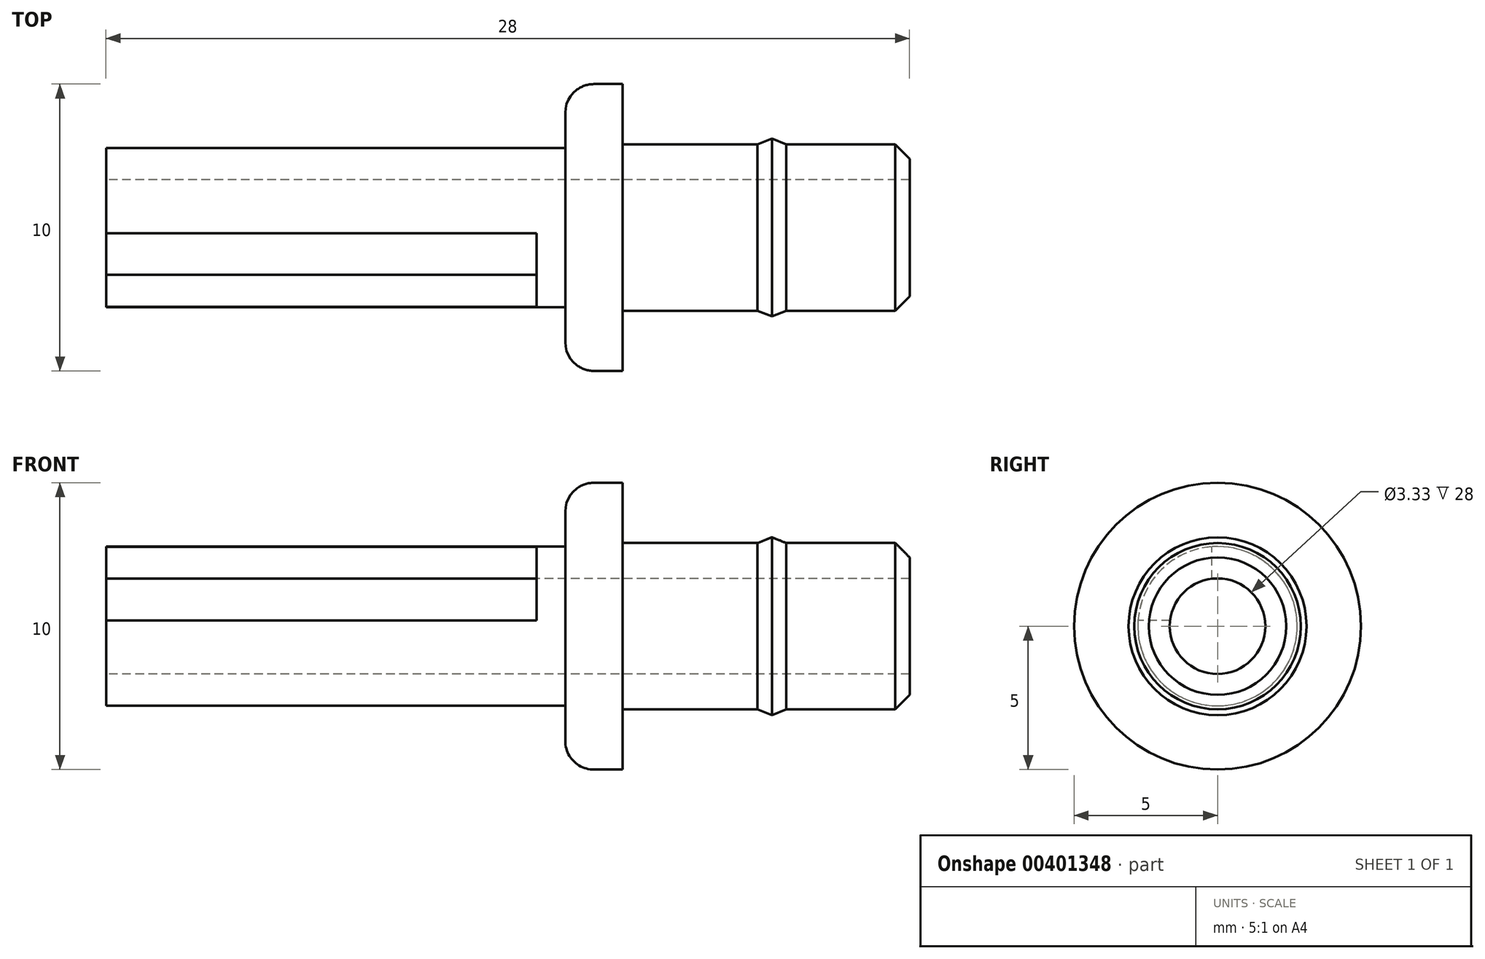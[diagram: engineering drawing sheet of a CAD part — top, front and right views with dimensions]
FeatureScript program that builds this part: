
annotation { "Feature Type Name" : "Feature", "Feature Type Description" : "" }
export const myFeature = defineFeature(function(context is Context, id is Id, definition is map)
    precondition{}
    {
        {
            var Q0;
            Q0=qCreatedBy(makeId("Front.planeOp"),FACE);
            var sketch = newSketch(context, id + "F0", { "sketchPlane" : qUnion([Q0])});
            skLineSegment(sketch, "E0", {"start": v(2.76, 1.67) * mm, "end": v(15.76, 1.67) * mm});
            skLineSegment(sketch, "E1", {"start": v(5.76, 2.9) * mm, "end": v(5.76, 5) * mm});
            skLineSegment(sketch, "E2", {"start": v(5.76, 5) * mm, "end": v(3.76, 5) * mm});
            skLineSegment(sketch, "E3", {"start": v(3.76, 5) * mm, "end": v(3.76, 2.78) * mm});
            skLineSegment(sketch, "E4", {"start": v(3.76, 2.78) * mm, "end": v(2.76, 2.78) * mm});
            skLineSegment(sketch, "E5", {"start": v(2.76, 2.78) * mm, "end": v(2.76, 1.67) * mm});
            skLineSegment(sketch, "E6", {"start": v(2.76, 0) * mm, "end": v(13.38, 0) * mm});
            skLineSegment(sketch, "E7", {"start": v(15.26, 2.9) * mm, "end": v(11.46, 2.9) * mm});
            skLineSegment(sketch, "E8", {"start": v(10.46, 2.9) * mm, "end": v(5.76, 2.9) * mm});
            skLineSegment(sketch, "E9", {"start": v(15.26, 2.9) * mm, "end": v(15.76, 2.4) * mm});
            skLineSegment(sketch, "E10", {"start": v(15.76, 2.4) * mm, "end": v(15.76, 1.67) * mm});
            skLineSegment(sketch, "E11", {"start": v(10.46, 2.9) * mm, "end": v(10.96, 3.1) * mm});
            skLineSegment(sketch, "E12", {"start": v(10.96, 3.1) * mm, "end": v(11.46, 2.9) * mm});
            skSolve(sketch);
        }
        {
            var Q0;
            Q0=makeQuery(id+"F0.imprint","IMPRINT",FACE,{"disambiguationData":[TD([[makeQuery(id+"F0.imprint","IMPRINT",EDGE,{"derivedFrom":sQuery(id+"F0.wireOp",EDGE,"E0")}),1.0]])]});
            var Q1;
            Q1=sQuery(id+"F0.wireOp",EDGE,"E6");
            revolve(context, id + "F1", {"entities" : qUnion([Q0]), "axis" : qUnion([Q1]), "revolveType" : RevolveType.FULL});
        }
        {
            var Q0;
            Q0=makeQuery(id+"F1.opRevolve","SWEPT_FACE",FACE,{"disambiguationData":[OSD([sQuery(id+"F0.wireOp",EDGE,"E5")])]});
            var sketch = newSketch(context, id + "F2", { "sketchPlane" : qUnion([Q0])});
            skLineSegment(sketch, "E13", {"start": v(-0.2, 1.65) * mm, "end": v(-0.2, 2.77) * mm});
            skLineSegment(sketch, "E14", {"start": v(-1.65, 0.2) * mm, "end": v(-2.77, 0.2) * mm});
            skArc(sketch, "E15", {"start": v(-2.77, 0.2) * mm, "mid": v(2.57, -1.06) * mm, "end": v(-2.1, 1.8) * mm});
            skArc(sketch, "E16", {"start": v(-1.19, 1.17) * mm, "mid": v(0.74, -1.5) * mm, "end": v(-0.2, 1.65) * mm});
            skLineSegment(sketch, "E17", {"start": v(0.2, 1.65) * mm, "end": v(0.2, 2.77) * mm});
            skLineSegment(sketch, "E18", {"start": v(1.65, 0.2) * mm, "end": v(2.77, 0.2) * mm});
            skArc(sketch, "E19", {"start": v(0.2, 1.65) * mm, "mid": v(-0.76, -1.48) * mm, "end": v(1.22, 1.14) * mm});
            skArc(sketch, "E20", {"start": v(0.2, 2.77) * mm, "mid": v(-1.12, -2.54) * mm, "end": v(1.92, 2) * mm});
            skLineSegment(sketch, "E21", {"start": v(-2.77, -0.2) * mm, "end": v(-1.65, -0.2) * mm});
            skLineSegment(sketch, "E22", {"start": v(-0.2, -1.65) * mm, "end": v(-0.2, -2.77) * mm});
            skLineSegment(sketch, "E23", {"start": v(1.65, -0.2) * mm, "end": v(2.77, -0.2) * mm});
            skLineSegment(sketch, "E24", {"start": v(0.2, -1.65) * mm, "end": v(0.2, -2.77) * mm});
            skSolve(sketch);
        }
        {
            var Q0;
            {var subQ5=sQuery(id+"F2.wireOp",EDGE,"E13");Q0=makeQuery(id+"F2.imprint","IMPRINT",FACE,{"disambiguationData":[TD([[makeQuery(id+"F2.imprint","IMPRINT",EDGE,{"derivedFrom":subQ5}),1.0]])]});}
            extrude(context, id + "F3", {"entities" : qUnion([Q0]), "operationType" : NewBodyOperationType.ADD, "depth" : 15 * mm});
        }
        {
            var Q0;
            {var subQ2=sQuery(id+"F2.wireOp",EDGE,"E15");Q0=makeQuery(id+"F2.imprint","IMPRINT",FACE,{"disambiguationData":[TD([[makeQuery(id+"F2.imprint","IMPRINT",EDGE,{"derivedFrom":subQ2}),1.0]])]});}
            extrude(context, id + "F4", {"entities" : qUnion([Q0]), "operationType" : NewBodyOperationType.ADD, "depth" : 15 * mm});
        }
        {
            var Q0;
            {var subQ0=sQuery(id+"F2.wireOp",EDGE,"E21");Q0=makeQuery(id+"F2.imprint","IMPRINT",FACE,{"disambiguationData":[TD([[makeQuery(id+"F2.imprint","IMPRINT",EDGE,{"derivedFrom":subQ0}),-1.0]])]});}
            extrude(context, id + "F5", {"entities" : qUnion([Q0]), "operationType" : NewBodyOperationType.ADD, "depth" : 15 * mm});
        }
        {
            var Q0;
            {var subQ0=sQuery(id+"F2.wireOp",EDGE,"E23");Q0=makeQuery(id+"F2.imprint","IMPRINT",FACE,{"disambiguationData":[TD([[makeQuery(id+"F2.imprint","IMPRINT",EDGE,{"derivedFrom":subQ0}),-1.0]])]});}
            extrude(context, id + "F6", {"entities" : qUnion([Q0]), "operationType" : NewBodyOperationType.ADD, "depth" : 15 * mm});
        }
        {
            var Q0;
            Q0=makeQuery(id+"F1.opRevolve","SWEPT_EDGE",EDGE,{"disambiguationData":[OSD([sQuery(id+"F0.wireOp",EDGE,"E2"),sQuery(id+"F0.wireOp",EDGE,"E3")])]});
            fillet(context, id + "F7", {"entities" : qUnion([Q0]), "radius" : 1 * mm, "tangentPropagation" : true, "allowEdgeOverflow" : false});
        }
    });
